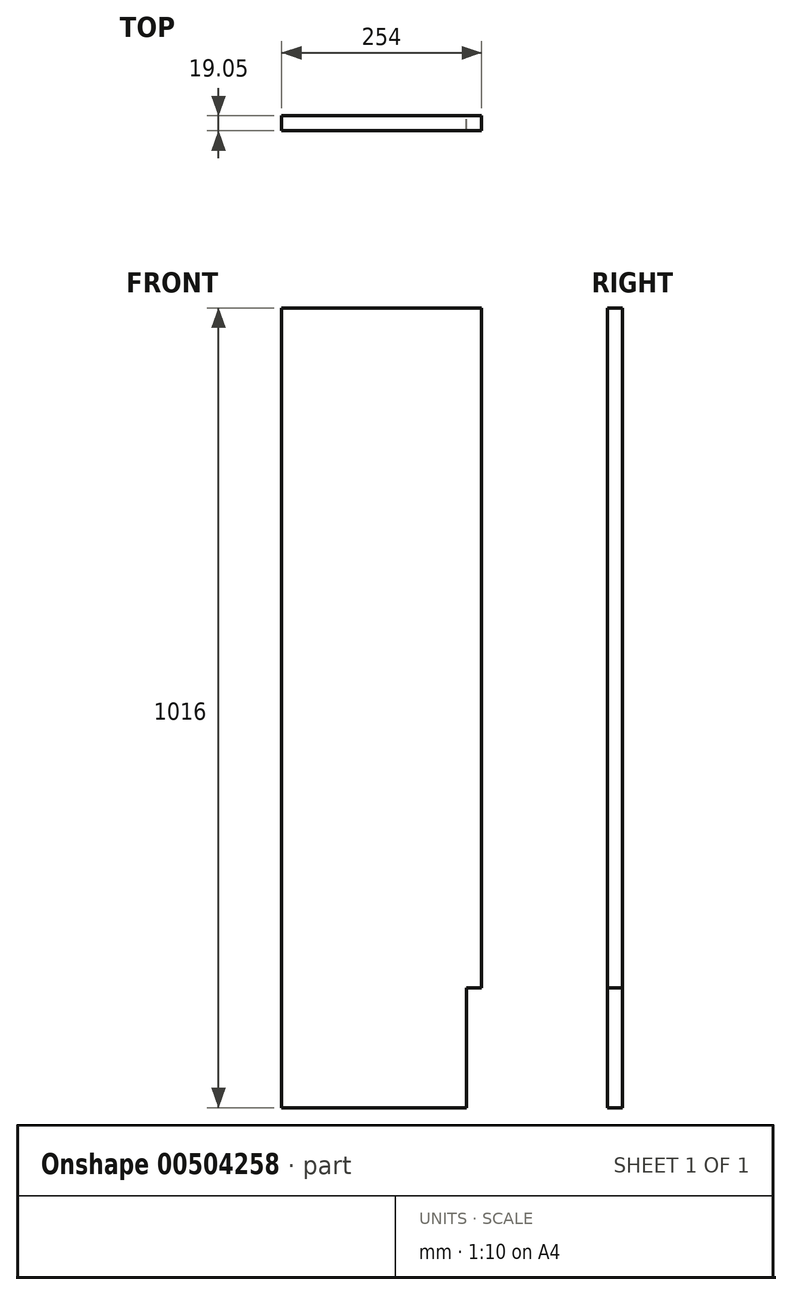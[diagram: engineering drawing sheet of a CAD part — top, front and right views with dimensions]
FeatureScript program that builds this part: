
annotation { "Feature Type Name" : "Feature", "Feature Type Description" : "" }
export const myFeature = defineFeature(function(context is Context, id is Id, definition is map)
    precondition{}
    {
        {
            var Q0;
            Q0=qCreatedBy(makeId("Front.planeOp"),FACE);
            var sketch = newSketch(context, id + "F0", { "sketchPlane" : qUnion([Q0])});
            skLineSegment(sketch, "E0.bottom", {"start": v(127, -508) * mm, "end": v(-127, -508) * mm});
            skLineSegment(sketch, "E0.top", {"start": v(127, 508) * mm, "end": v(-127, 508) * mm});
            skLineSegment(sketch, "E0.left", {"start": v(127, -508) * mm, "end": v(127, 508) * mm});
            skLineSegment(sketch, "E0.right", {"start": v(-127, -508) * mm, "end": v(-127, 508) * mm});
            skPoint(sketch, "E0.middle", {"position": v(0, 0) * mm});
            skLineSegment(sketch, "E1.bottom", {"start": v(127, -508) * mm, "end": v(107.95, -508) * mm});
            skLineSegment(sketch, "E1.top", {"start": v(127, -355.6) * mm, "end": v(107.95, -355.6) * mm});
            skLineSegment(sketch, "E1.left", {"start": v(127, -508) * mm, "end": v(127, -355.6) * mm});
            skLineSegment(sketch, "E1.right", {"start": v(107.95, -508) * mm, "end": v(107.95, -355.6) * mm});
            skSolve(sketch);
        }
        {
            var Q0;
            {var subQ1=sQuery(id+"F0.wireOp",EDGE,"E0.top");Q0=makeQuery(id+"F0.imprint","IMPRINT",FACE,{"disambiguationData":[TD([[makeQuery(id+"F0.imprint","IMPRINT",EDGE,{"derivedFrom":subQ1}),1.0]])]});}
            extrude(context, id + "F1", {"entities" : qUnion([Q0]), "depth" : 19.05 * mm});
        }
    });
